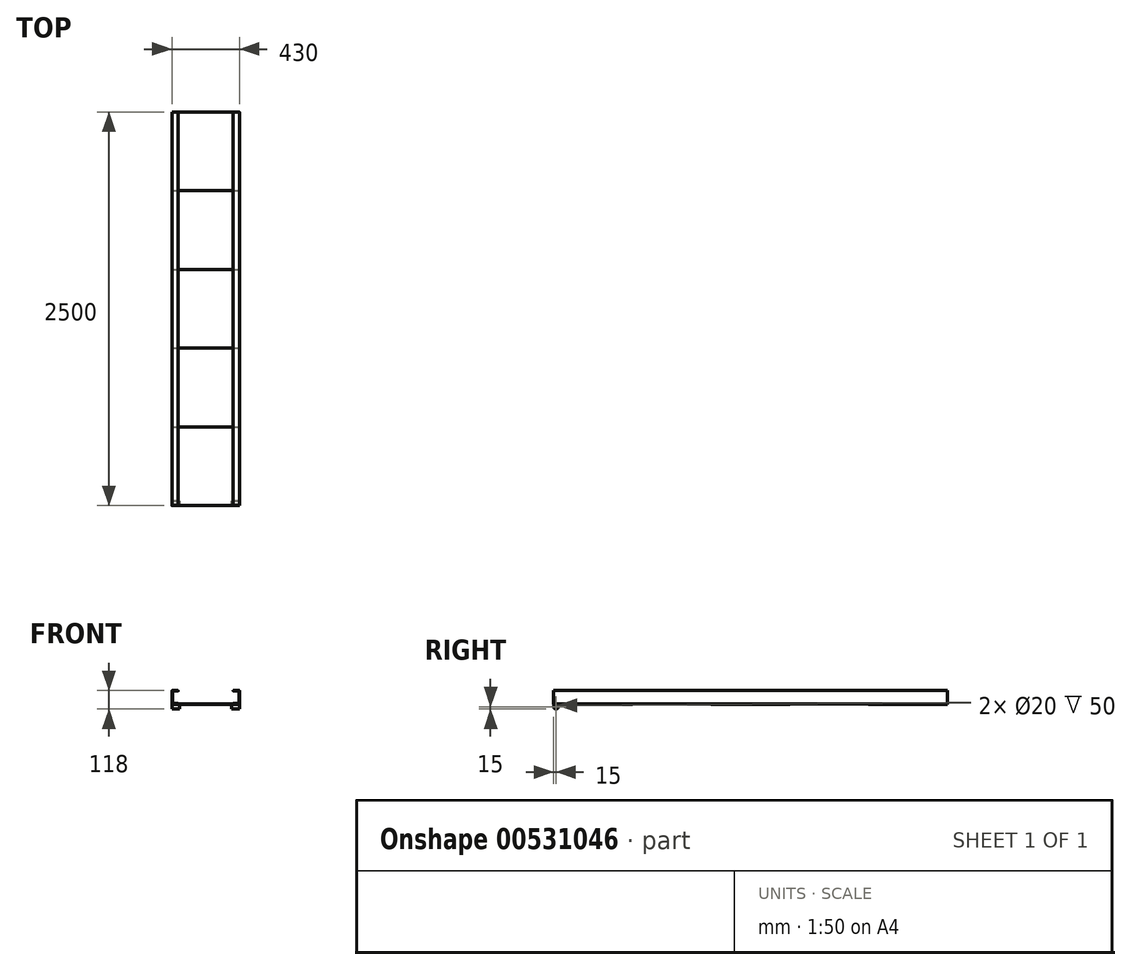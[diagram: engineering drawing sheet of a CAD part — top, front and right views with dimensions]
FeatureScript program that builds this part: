
annotation { "Feature Type Name" : "Feature", "Feature Type Description" : "" }
export const myFeature = defineFeature(function(context is Context, id is Id, definition is map)
    precondition{}
    {
        {
            var Q0;
            Q0=qCreatedBy(makeId("Front.planeOp"),FACE);
            var sketch = newSketch(context, id + "F0", { "sketchPlane" : qUnion([Q0])});
            skLineSegment(sketch, "E0", {"start": v(-176, 42.5) * mm, "end": v(-214, 42.5) * mm});
            skLineSegment(sketch, "E1", {"start": v(-215, 41.5) * mm, "end": v(-215, -41.5) * mm});
            skLineSegment(sketch, "E2", {"start": v(-214, -42.5) * mm, "end": v(-176, -42.5) * mm});
            skLineSegment(sketch, "E3", {"start": v(-175, -41.5) * mm, "end": v(-175, -39.5) * mm});
            skLineSegment(sketch, "E4", {"start": v(-176, -38.5) * mm, "end": v(-210, -38.5) * mm});
            skLineSegment(sketch, "E5", {"start": v(-211, -37.5) * mm, "end": v(-211, 37.5) * mm});
            skLineSegment(sketch, "E6", {"start": v(-210, 38.5) * mm, "end": v(-176, 38.5) * mm});
            skLineSegment(sketch, "E7", {"start": v(-175, 39.5) * mm, "end": v(-175, 41.5) * mm});
            skPoint(sketch, "E8", {"position": v(-215, 0) * mm});
            skPoint(sketch, "E9.visualSharp", {"position": v(-215, 42.5) * mm});
            skArc(sketch, "E9.filletArc", {"start": v(-214, 42.5) * mm, "mid": v(-214.7, 42.2) * mm, "end": v(-215, 41.5) * mm});
            skPoint(sketch, "E10.visualSharp", {"position": v(-175, 42.5) * mm});
            skArc(sketch, "E10.filletArc", {"start": v(-175, 41.5) * mm, "mid": v(-175.3, 42.2) * mm, "end": v(-176, 42.5) * mm});
            skPoint(sketch, "E11.visualSharp", {"position": v(-175, 38.5) * mm});
            skArc(sketch, "E11.filletArc", {"start": v(-176, 38.5) * mm, "mid": v(-175.3, 38.8) * mm, "end": v(-175, 39.5) * mm});
            skPoint(sketch, "E12.visualSharp", {"position": v(-175, -38.5) * mm});
            skArc(sketch, "E12.filletArc", {"start": v(-175, -39.5) * mm, "mid": v(-175.3, -38.8) * mm, "end": v(-176, -38.5) * mm});
            skPoint(sketch, "E13.visualSharp", {"position": v(-175, -42.5) * mm});
            skArc(sketch, "E13.filletArc", {"start": v(-176, -42.5) * mm, "mid": v(-175.3, -42.2) * mm, "end": v(-175, -41.5) * mm});
            skPoint(sketch, "E14.visualSharp", {"position": v(-211, -38.5) * mm});
            skArc(sketch, "E14.filletArc", {"start": v(-211, -37.5) * mm, "mid": v(-210.7, -38.2) * mm, "end": v(-210, -38.5) * mm});
            skPoint(sketch, "E15.visualSharp", {"position": v(-215, -42.5) * mm});
            skArc(sketch, "E15.filletArc", {"start": v(-215, -41.5) * mm, "mid": v(-214.7, -42.2) * mm, "end": v(-214, -42.5) * mm});
            skPoint(sketch, "E16.visualSharp", {"position": v(-211, 38.5) * mm});
            skArc(sketch, "E16.filletArc", {"start": v(-210, 38.5) * mm, "mid": v(-210.7, 38.2) * mm, "end": v(-211, 37.5) * mm});
            skArc(sketch, "E17.MirrorCS", {"start": v(176, -42.5) * mm, "mid": v(175.3, -42.2) * mm, "end": v(175, -41.5) * mm});
            skArc(sketch, "E18.MirrorCS", {"start": v(175, -39.5) * mm, "mid": v(175.3, -38.8) * mm, "end": v(176, -38.5) * mm});
            skArc(sketch, "E19.MirrorCS", {"start": v(176, 38.5) * mm, "mid": v(175.3, 38.8) * mm, "end": v(175, 39.5) * mm});
            skArc(sketch, "E20.MirrorCS", {"start": v(210, 38.5) * mm, "mid": v(210.7, 38.2) * mm, "end": v(211, 37.5) * mm});
            skArc(sketch, "E21.MirrorCS", {"start": v(215, -41.5) * mm, "mid": v(214.7, -42.2) * mm, "end": v(214, -42.5) * mm});
            skArc(sketch, "E22.MirrorCS", {"start": v(175, 41.5) * mm, "mid": v(175.3, 42.2) * mm, "end": v(176, 42.5) * mm});
            skArc(sketch, "E23.MirrorCS", {"start": v(214, 42.5) * mm, "mid": v(214.7, 42.2) * mm, "end": v(215, 41.5) * mm});
            skLineSegment(sketch, "E24.MirrorCS", {"start": v(175, 39.5) * mm, "end": v(175, 41.5) * mm});
            skArc(sketch, "E25.MirrorCS", {"start": v(211, -37.5) * mm, "mid": v(210.7, -38.2) * mm, "end": v(210, -38.5) * mm});
            skLineSegment(sketch, "E26.MirrorCS", {"start": v(175, -41.5) * mm, "end": v(175, -39.5) * mm});
            skPoint(sketch, "E27.MirrorP", {"position": v(175, -38.5) * mm});
            skPoint(sketch, "E28.MirrorP", {"position": v(175, -42.5) * mm});
            skPoint(sketch, "E29.MirrorP", {"position": v(175, 38.5) * mm});
            skPoint(sketch, "E30.MirrorP", {"position": v(175, 42.5) * mm});
            skPoint(sketch, "E31.MirrorP", {"position": v(211, -38.5) * mm});
            skPoint(sketch, "E32.MirrorP", {"position": v(215, 42.5) * mm});
            skPoint(sketch, "E33.MirrorP", {"position": v(211, 38.5) * mm});
            skLineSegment(sketch, "E34.MirrorCS", {"start": v(176, 42.5) * mm, "end": v(214, 42.5) * mm});
            skLineSegment(sketch, "E35.MirrorCS", {"start": v(215, 41.5) * mm, "end": v(215, -41.5) * mm});
            skPoint(sketch, "E36.MirrorP", {"position": v(215, -42.5) * mm});
            skLineSegment(sketch, "E37.MirrorCS", {"start": v(211, -37.5) * mm, "end": v(211, 37.5) * mm});
            skLineSegment(sketch, "E38.MirrorCS", {"start": v(214, -42.5) * mm, "end": v(176, -42.5) * mm});
            skPoint(sketch, "E39.MirrorP", {"position": v(215, 0) * mm});
            skLineSegment(sketch, "E40.MirrorCS", {"start": v(176, -38.5) * mm, "end": v(210, -38.5) * mm});
            skLineSegment(sketch, "E41.MirrorCS", {"start": v(210, 38.5) * mm, "end": v(176, 38.5) * mm});
            skSolve(sketch);
        }
        {
            var Q0;
            Q0 = qSketchRegion(id + "F0", true);
            extrude(context, id + "F1", {"entities" : qUnion([Q0]), "depth" : 2500 * mm, "offsetDistance" : 25 * mm});
        }
        {
            var Q0;
            Q0=makeQuery(id+"F1.opExtrude","SWEPT_FACE",FACE,{"disambiguationData":[OSD([sQuery(id+"F0.wireOp",EDGE,"E38.MirrorCS")])]});
            var sketch = newSketch(context, id + "F2", { "sketchPlane" : qUnion([Q0])});
            skLineSegment(sketch, "E42.bottom", {"start": v(-215, 2500) * mm, "end": v(215, 2500) * mm});
            skLineSegment(sketch, "E42.top", {"start": v(-215, 2000) * mm, "end": v(215, 2000) * mm});
            skLineSegment(sketch, "E42.left", {"start": v(-215, 2500) * mm, "end": v(-215, 2000) * mm});
            skLineSegment(sketch, "E42.right", {"start": v(215, 2500) * mm, "end": v(215, 2000) * mm});
            skLineSegment(sketch, "E43.bottom", {"start": v(-215, 1500) * mm, "end": v(215, 1500) * mm});
            skLineSegment(sketch, "E43.top", {"start": v(-215, 1000) * mm, "end": v(215, 1000) * mm});
            skLineSegment(sketch, "E43.left", {"start": v(-215, 1500) * mm, "end": v(-215, 1000) * mm});
            skLineSegment(sketch, "E43.right", {"start": v(215, 1500) * mm, "end": v(215, 1000) * mm});
            skLineSegment(sketch, "E44.bottom", {"start": v(-215, 500) * mm, "end": v(215, 500) * mm});
            skLineSegment(sketch, "E44.top", {"start": v(-215, 0) * mm, "end": v(215, 0) * mm});
            skLineSegment(sketch, "E44.left", {"start": v(-215, 500) * mm, "end": v(-215, 0) * mm});
            skLineSegment(sketch, "E44.right", {"start": v(215, 500) * mm, "end": v(215, 0) * mm});
            skPoint(sketch, "E45", {"position": v(0, 0) * mm});
            skSolve(sketch);
        }
        {
            var Q0;
            Q0 = qSketchRegion(id + "F2", true);
            extrude(context, id + "F3", {"entities" : qUnion([Q0]), "depth" : 3 * mm, "offsetDistance" : 25 * mm});
        }
        {
            var Q0;
            Q0=makeQuery(id+"F1.opExtrude","SWEPT_FACE",FACE,{"disambiguationData":[OSD([sQuery(id+"F0.wireOp",EDGE,"E1")])]});
            var sketch = newSketch(context, id + "F4", { "sketchPlane" : qUnion([Q0])});
            skCircle(sketch, "E46", {"center": v(2485, -60.5) * mm, "radius": 10 * mm});
            skArc(sketch, "E47", {"start": v(2474.5, -49.79) * mm, "mid": v(2485, -75.5) * mm, "end": v(2495.5, -49.79) * mm});
            skLineSegment(sketch, "E48", {"start": v(2472.75, -45.5) * mm, "end": v(2497.25, -45.5) * mm});
            skLineSegment(sketch, "E49", {"start": v(2500, -45.5) * mm, "end": v(2500, -114.34) * mm, "construction": true});
            skArc(sketch, "E50", {"start": v(2474.5, -49.79) * mm, "mid": v(2475.07, -47.06) * mm, "end": v(2472.75, -45.5) * mm});
            skArc(sketch, "E51", {"start": v(2497.25, -45.5) * mm, "mid": v(2494.93, -47.06) * mm, "end": v(2495.5, -49.79) * mm});
            skSolve(sketch);
        }
        {
            var Q0;
            Q0 = qSketchRegion(id + "F4", true);
            var Q1;
            Q1=makeQuery(id+"F1.opExtrude","SWEPT_FACE",FACE,{"disambiguationData":[OSD([sQuery(id+"F0.wireOp",EDGE,"E35.MirrorCS")])]});
            extrude(context, id + "F5", {"entities" : qUnion([Q0]), "operationType" : NewBodyOperationType.ADD, "endBound" : BoundingType.UP_TO_SURFACE, "oppositeDirection" : true, "depth" : 25 * mm, "endBoundEntityFace" : qUnion([Q1]), "offsetDistance" : 25 * mm});
        }
        {
            var Q0;
            Q0=makeQuery(id+"F3.opExtrude","SWEPT_FACE",FACE,{"disambiguationData":[OSD([sQuery(id+"F2.wireOp",EDGE,"E42.bottom")])]});
            var sketch = newSketch(context, id + "F6", { "sketchPlane" : qUnion([Q0])});
            skLineSegment(sketch, "E52.bottom", {"start": v(-165, -81.22) * mm, "end": v(165, -81.22) * mm});
            skLineSegment(sketch, "E52.top", {"start": v(-165, -45.5) * mm, "end": v(165, -45.5) * mm});
            skLineSegment(sketch, "E52.left", {"start": v(-165, -81.22) * mm, "end": v(-165, -45.5) * mm});
            skLineSegment(sketch, "E52.right", {"start": v(165, -81.22) * mm, "end": v(165, -45.5) * mm});
            skSolve(sketch);
        }
        {
            var Q0;
            Q0 = qSketchRegion(id + "F6", true);
            extrude(context, id + "F7", {"entities" : qUnion([Q0]), "operationType" : NewBodyOperationType.REMOVE, "oppositeDirection" : true, "depth" : 49 * mm, "offsetDistance" : 25 * mm});
        }
    });
